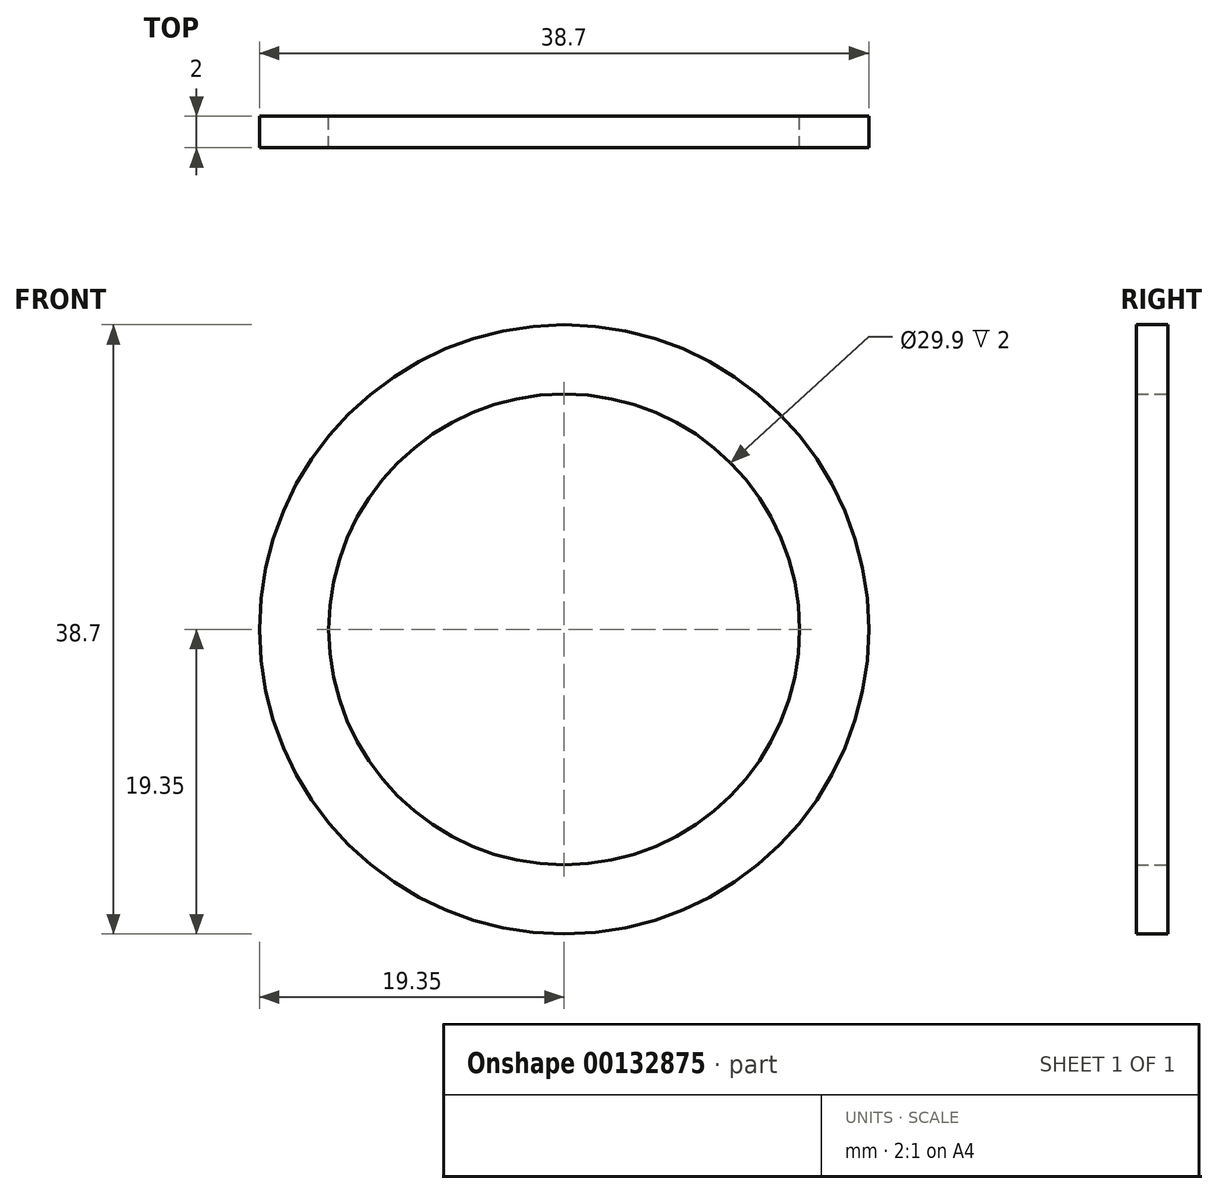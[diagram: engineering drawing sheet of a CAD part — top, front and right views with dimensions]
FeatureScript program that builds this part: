
annotation { "Feature Type Name" : "Feature", "Feature Type Description" : "" }
export const myFeature = defineFeature(function(context is Context, id is Id, definition is map)
    precondition{}
    {
        {
            var Q0;
            Q0=qCreatedBy(makeId("Front.planeOp"),FACE);
            var sketch = newSketch(context, id + "F0", { "sketchPlane" : qUnion([Q0])});
            skCircle(sketch, "E0", {"center": v(0, 0) * mm, "radius": 19.35 * mm});
            skCircle(sketch, "E1", {"center": v(0, 0) * mm, "radius": 14.95 * mm});
            skSolve(sketch);
        }
        {
            var Q0;
            Q0 = qSketchRegion(id + "F0", true);
            extrude(context, id + "F1", {"entities" : qUnion([Q0]), "depth" : 2 * mm});
        }
    });
